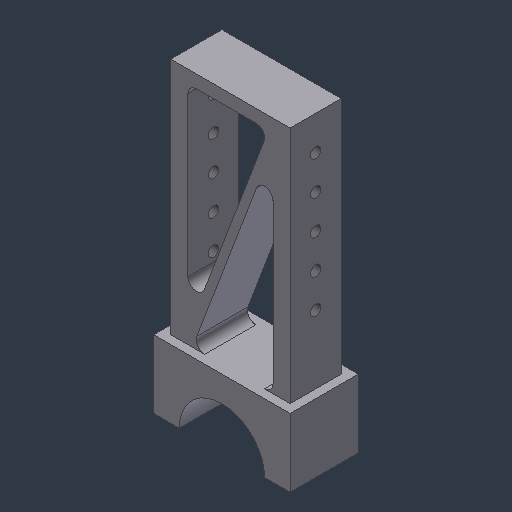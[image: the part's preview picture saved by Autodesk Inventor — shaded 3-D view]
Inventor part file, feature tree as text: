
AUTODESK INVENTOR PART (.ipt)
format: ipt  version: 2024.3 (Build 283343000, 343)  size: 224,768 bytes
history: native  units: mm (DEFAULTED — no unit token found)
features: sketch x5, hole x3, extrude x2, fillet x1, mirror x1
ambient origin geometry x8: Origin, YZ Plane, XZ Plane, XY Plane, X Axis, Y Axis, Z Axis, Center Point
bodies: Solid1 (feature_tree)
feature tree (12):
  extrude  "Extrusion1"  Depth=88.9mm
  hole  "Hole1"  [1 undecoded]
  fillet  "Fillet1"  Radius=25.4mm
  hole  "Hole2"  [1 undecoded]
  mirror  "Mirror1"
  extrude  "Extrusion2"  Depth=3.175mm
  hole  "Hole3"  [1 undecoded]
  sketch  "Sketch2"  dims[d0=44.45mm d1=88.9mm]
  sketch  "Sketch4"  dims[d2=25.4mm d3=25.4mm d4=25.4mm d5=0.0mm]
  sketch  "Sketch5"  dims[d6=6.35mm d7=4.7625mm]
  sketch  "Sketch6"  dims[d8=1.5875mm]
  sketch  "Sketch7"  dims[d9=31.75mm d10=9.525mm d11=9.525mm d12=6.35mm d13=14.3117mm d14=12.7mm d15=20.594885mm d16=3.175mm d19=50.0mm d21=12.7mm d22=10.0mm d24=25.4mm d26=3.9624mm d27=9.652mm d28=9.525mm d29=6.35mm d30=14.3117mm d31=13.6144mm d32=20.594885mm d33=25.4mm d34=19.05mm d35=0.0mm d36=0.0mm d37=25.4mm d39=12.7mm d40=41.275mm d41=3.9624mm d42=9.652mm d43=9.525mm d44=6.35mm d45=14.3117mm d46=13.6144mm d47=20.594885mm]
note: 3 required parameter values undecoded (feature->parameter linkage not recoverable at this tier; creation-order binding heuristic only, values carry confidence <= 0.55)
